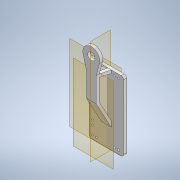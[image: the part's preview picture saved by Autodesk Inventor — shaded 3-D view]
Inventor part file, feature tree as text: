
AUTODESK INVENTOR PART (.ipt)
format: ipt  version: 2022 (Build 260153000, 153)  size: 210,432 bytes
history: native  units: mm
features: other x7, extrude x4, sketch x3, reference x1
ambient origin geometry x8: Origin, YZ Plane, XZ Plane, XY Plane, X Axis, Y Axis, Z Axis, Center Point
bodies: Body1 (feature_tree)
feature tree (15):
  other  "Твердое тело1"
  other  "РабПлоскость1"
  extrude  "Выдавливание1"  Depth=2.5mm TaperAngle=0.0deg
  other  "РабПлоскость4"
  extrude  "Выдавливание5"  Depth=6.0mm
  other  "РабПлоскость5"
  sketch  "Эскиз8"
  extrude  "Выдавливание6"  Depth=12.0mm
  extrude  "Выдавливание7"  Depth=7.0mm
  sketch  "Эскиз1"
  reference  "Ссылка1"
  sketch  "Эскиз7"
  other  "<userpath>\Documents\Inventor\AIM\Aim.iam"
  other  "Aim.iam"
  other  "Base:2"
